# Revit family: DSP_A3-AF01A
name_source: partatom
category: Doors
revit_build: Autodesk Revit 2016 (Build: 20150220_1215(x64)
units: mm (PartAtom-declared; Revit-internal decimal feet)

## family parameters
Always vertical = Yes
Cut with Voids When Loaded = No
Host = Wall
Room Calculation Point = No
Shared = No

## types (1)
- Wc Alumn Frame for 813 x 2032mm
    Construction Type = AF01
    Description = Standard Door
    Door Frame = Extruded aluminium section to comply with AAAMSA specification and complete as supplied by manufacturer. No top frame. Side frames only with capped edges.
    Door Frame Finish = Aluminium Finish
    Door Panel = Standard Semi-solid Medium Duty flush panel door leaf. 40mm thick with masonite veneer faces suitable for painting and edges to match veneer.
    Door Panel Finish = Stop with polyfilla spackle. Ensure that surfaces to be coated are clean, dry, firm and dust free. Apply 2-3 coats paint as specified.
    Door panel Height = 1980 mm  [stored 6.49606 ft]
    Frame Centre = 58 mm
    Function = Interior
    Height = 2125 mm  [stored 6.97178 ft]
    Manufacturer = Aluminium Manufacturer
    Note = All quantities & dimensions to be checked on site by contractor prior to ordering of any material, final quantities to be verified by architect. Schedules to be read in conjunction with latest floor layout drawings & finishing schedules.
    Other = Hinges as supplied by manufacturer. Manufacturer to take note of door weight and to supply hinges accordingly.
    Panel Height = 1980
    Panel Width = 813
    Wall Closure = By host
    Width = 873 mm  [stored 2.86417 ft]

note: [stored X ft] marks values corroborated as IEEE doubles in the binary element streams (Revit-internal decimal feet)

## geometry (parser evidence)
native form markers: Sweep x5
no freeform markers — native parametric forms only
